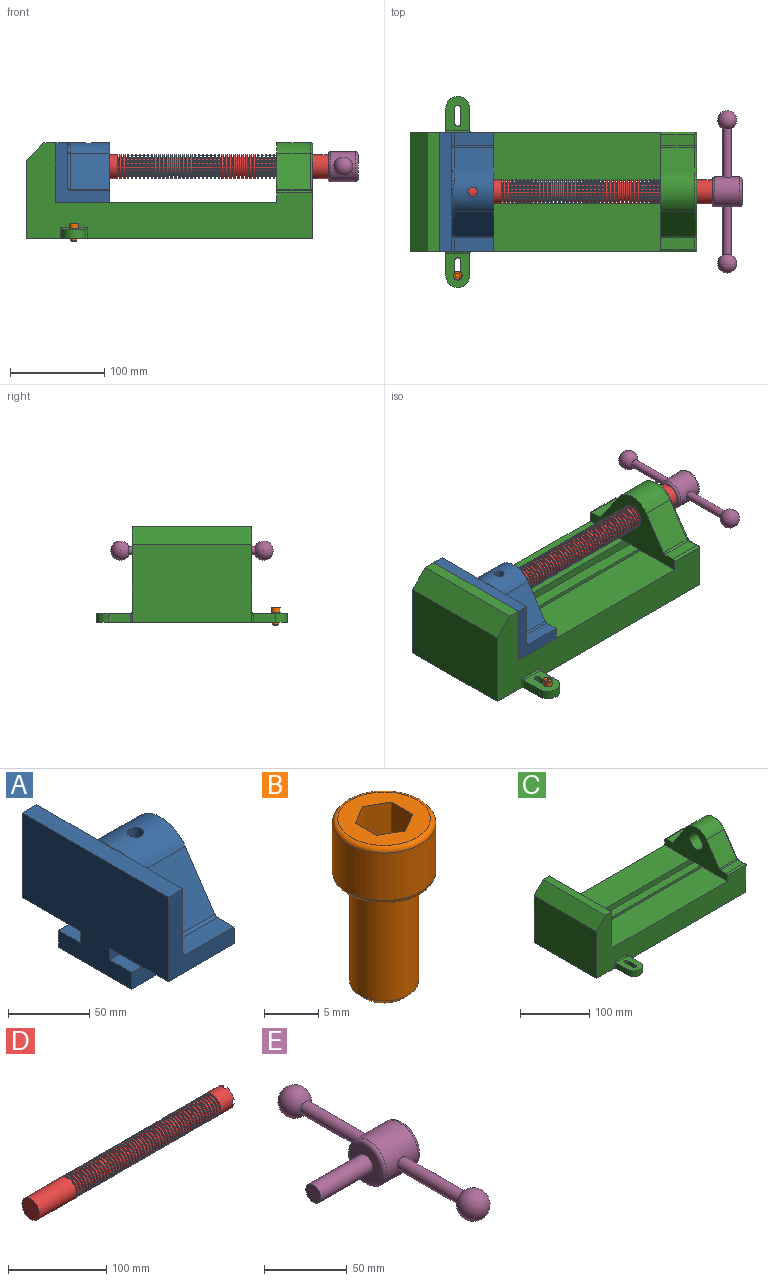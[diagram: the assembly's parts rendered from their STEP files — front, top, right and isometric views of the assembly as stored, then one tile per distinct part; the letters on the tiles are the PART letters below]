
ASSEMBLY  parts=5 mates=5
PART A: 36 faces, bbox 57.2x127x89 mm
  f0: plane 57.15x50.8mm, normal (0,0,-1), area 2903.2mm2, adj f6,f9,f10,f23
  f1: cylinder r=12.7mm len=44.45mm, axis (1,0,0), area 3464.3mm2, adj f6,f15,f16
  f2: plane 41.91x14.52mm, normal (0,0,1), area 608.5mm2, adj f6,f11,f24,f25
  f3: plane 51.86x48.26mm, normal (1,0,0), area 1495.7mm2, adj f8,f10,f31,f33,f35
  f4: plane 51.86x48.26mm, normal (1,0,0), area 1495.7mm2, adj f8,f11,f24,f28,f29
  f5: plane 57.15x50.8mm, normal (0,0,-1), area 2903.2mm2, adj f6,f9,f11,f22
  f6: plane 127x85.09mm, normal (1,0,0), area 5190.6mm2, adj f0,f1,f2,f5,f7,f10,f11,f12
  f7: plane 41.91x14.52mm, normal (0,0,1), area 608.5mm2, adj f6,f10,f30,f31
  f8: plane 127x12.7mm, normal (0,0,1), area 1612.9mm2, adj f3,f4,f9,f10,f11,f26,f34
  f9: plane 127x85.09mm, normal (-1,0,0), area 9096.8mm2, adj f0,f5,f8,f10,f11,f17,f18,f19
  f10: plane 63.5x57.15mm, normal (0,-1,0), area 1372.3mm2, adj f0,f3,f6,f7,f8,f9,f31
  f11: plane 63.5x57.15mm, normal (0,1,0), area 1372.3mm2, adj f2,f4,f5,f6,f8,f9,f24
  f12: plane 41.91x38.43mm, normal (0,-0.83,0.56), area 1939.2mm2, adj f6,f13,f30,f33
  f13: cylinder r=25.4mm len=44.45mm, axis (1,0,0), area 2026.5mm2, adj f6,f12,f14,f16,f26,f28,f34,f35
  f14: plane 41.91x38.43mm, normal (0,0.83,0.56), area 1939.2mm2, adj f6,f13,f25,f29
  f15: plane 25.4x25.4mm, normal (1,0,0), area 506.7mm2, adj f1
  f16: cylinder r=5.08mm len=13.76mm, axis (0,0,1), area 414mm2, adj f1,f13
  f17: plane 57.15x19.05mm, normal (0,0,1), area 1088.7mm2, adj f6,f9,f18,f23
  f18: plane 57.15x12.7mm, normal (0,-1,0), area 725.8mm2, adj f6,f9,f17,f19
  f19: plane 63.5x57.15mm, normal (0,0,-1), area 3629mm2, adj f6,f9,f18,f20
  f20: plane 57.15x12.7mm, normal (0,1,0), area 725.8mm2, adj f6,f9,f19,f21
  f21: plane 57.15x19.05mm, normal (0,0,1), area 1088.7mm2, adj f6,f9,f20,f22
  f22: plane 57.15x8.89mm, normal (0,1,0), area 508.1mm2, adj f5,f6,f9,f21
  f23: plane 57.15x8.89mm, normal (0,-1,0), area 508.1mm2, adj f0,f6,f9,f17
  f24: cylinder r=2.54mm len=14.52mm, axis (0,-1,0), area 57.9mm2, adj f2,f4,f11,f27
  f25: cylinder r=2.54mm len=41.91mm, axis (1,0,0), area 104.3mm2, adj f2,f6,f14,f27
  f26: bspline ~12.24x2.8mm, area 20.9mm2, adj f8,f13,f28
  f27: sphere r=2.54mm, area 6.3mm2, adj f24,f25,f29
  f28: torus R=27.94mm, axis (1,0,0), area 57.8mm2, adj f4,f13,f26,f29
  f29: cylinder r=2.54mm len=39.84mm, axis (0,-0.56,0.83), area 184.6mm2, adj f4,f14,f27,f28
  f30: cylinder r=2.54mm len=41.91mm, axis (1,0,0), area 104.3mm2, adj f6,f7,f12,f32
  f31: cylinder r=2.54mm len=14.52mm, axis (0,-1,0), area 57.9mm2, adj f3,f7,f10,f32
  f32: sphere r=2.54mm, area 6.3mm2, adj f30,f31,f33
  f33: cylinder r=2.54mm len=39.84mm, axis (0,-0.56,-0.83), area 184.6mm2, adj f3,f12,f32,f35
  f34: bspline ~12.24x2.8mm, area 20.9mm2, adj f8,f13,f35
  f35: torus R=27.94mm, axis (1,0,0), area 57.8mm2, adj f3,f13,f33,f34
PART B: 15 faces, bbox 10.3x10.3x19.1 mm
  f0: plane 8.51x8.51mm, normal (0,0,1), area 37.2mm2, adj f5,f6,f7,f8,f9,f10,f14
  f1: cylinder r=3.17mm len=11.94mm, axis (0,0,1), area 238.2mm2, adj f4,f12
  f2: plane 4.83x4.83mm, normal (0,0,-1), area 18.3mm2, adj f12
  f3: cylinder r=4.76mm len=9.53mm, axis (0,0,-1), area 159.6mm2, adj f13,f14
  f4: plane 8.51x8.51mm, normal (0,0,-1), area 25.2mm2, adj f1,f13
  f5: plane 4.83x2.38mm, normal (-0.5,-0.87,0), area 13.3mm2, adj f0,f6,f10,f11
  f6: plane 4.83x2.38mm, normal (0.5,-0.87,0), area 13.3mm2, adj f0,f5,f7,f11
  f7: plane 4.83x2.75mm, normal (1,0,0), area 13.3mm2, adj f0,f6,f8,f11
  f8: plane 4.83x2.38mm, normal (0.5,0.87,0), area 13.3mm2, adj f0,f7,f9,f11
  f9: plane 4.83x2.38mm, normal (-0.5,0.87,0), area 13.3mm2, adj f0,f8,f10,f11
  f10: plane 4.83x2.75mm, normal (-1,0,0), area 13.3mm2, adj f0,f5,f9,f11
  f11: plane 5.5x4.76mm, normal (0,0,1), area 19.6mm2, adj f5,f6,f7,f8,f9,f10
  f12: cone r=3.17mm half-angle=45deg, axis (0,0,1), area 18.9mm2, adj f1,f2
  f13: torus R=4.25mm, axis (0,0,1), area 23mm2, adj f3,f4
  f14: torus R=4.25mm, axis (0,0,1), area 23mm2, adj f0,f3
PART C: 61 faces, bbox 304.8x203.2x103.7 mm
  f0: plane 304.8x101.6mm, normal (0,1,0), area 13520.3mm2, adj f3,f4,f5,f6,f7,f8,f9,f16
  f1: plane 304.8x101.6mm, normal (0,-1,0), area 13520.3mm2, adj f2,f3,f5,f6,f7,f8,f9,f16
  f2: plane 234.95x50.8mm, normal (0,0,1), area 11935.5mm2, adj f1,f5,f16,f26
  f3: plane 127x99.06mm, normal (1,0,0), area 7097.5mm2, adj f0,f1,f9,f14,f17,f18,f19,f20
  f4: plane 234.95x50.8mm, normal (0,0,1), area 11935.5mm2, adj f0,f5,f16,f27
  f5: plane 127x101.6mm, normal (1,0,0), area 9516.1mm2, adj f0,f1,f2,f4,f6,f9,f18,f19
  f6: plane 127x12.7mm, normal (0,0,1), area 1612.9mm2, adj f0,f1,f5,f7
  f7: plane 127x19.05mm, normal (-0.71,0,0.71), area 3421.5mm2, adj f0,f1,f6,f8
  f8: plane 127x82.55mm, normal (-1,0,0), area 10483.8mm2, adj f0,f1,f7,f9
  f9: plane 304.8x203.2mm, normal (0,0,-1), area 33298.3mm2, adj f0,f1,f3,f5,f8,f21,f22,f39
  f10: plane 35.56x11.98mm, normal (0,0,1), area 426mm2, adj f16,f28,f29,f30
  f11: plane 38.43x35.56mm, normal (0,0.83,0.56), area 1645.4mm2, adj f12,f16,f29,f32
  f12: cylinder r=25.4mm len=42.19mm, axis (1,0,0), area 1770.2mm2, adj f11,f13,f16,f33
  f13: plane 38.43x35.56mm, normal (0,-0.83,0.56), area 1645.4mm2, adj f12,f16,f34,f35
  f14: cylinder r=12.7mm len=38.1mm, axis (1,0,0), area 3040.2mm2, adj f3,f16
  f15: plane 35.56x11.98mm, normal (0,0,1), area 426mm2, adj f16,f34,f36,f38
  f16: plane 127x63.5mm, normal (-1,0,0), area 4155.5mm2, adj f0,f1,f2,f4,f10,f11,f12,f13
  f17: plane 38.1x25.4mm, normal (0,0,-1), area 967.7mm2, adj f3,f16,f26,f27
  f18: plane 273.05x19.05mm, normal (0,0,-1), area 5201.6mm2, adj f3,f5,f19,f26
  f19: plane 273.05x12.7mm, normal (0,1,0), area 3467.7mm2, adj f3,f5,f18,f20
  f20: plane 273.05x19.05mm, normal (0,0,1), area 5201.6mm2, adj f3,f5,f19,f21
  f21: plane 273.05x16.51mm, normal (0,1,0), area 4508.1mm2, adj f3,f5,f9,f20
  f22: plane 273.05x16.51mm, normal (0,-1,0), area 4508.1mm2, adj f3,f5,f9,f23
  f23: plane 273.05x19.05mm, normal (0,0,1), area 5201.6mm2, adj f3,f5,f22,f24
  f24: plane 273.05x12.7mm, normal (0,-1,0), area 3467.7mm2, adj f3,f5,f23,f25
  f25: plane 273.05x19.05mm, normal (0,0,-1), area 5201.6mm2, adj f3,f5,f24,f27
  f26: plane 273.05x8.89mm, normal (0,1,0), area 2427.4mm2, adj f2,f3,f5,f17,f18
  f27: plane 273.05x8.89mm, normal (0,-1,0), area 2427.4mm2, adj f3,f4,f5,f17,f25
  f28: cylinder r=2.54mm len=38.1mm, axis (1,0,0), area 148.3mm2, adj f0,f10,f16,f30
  f29: cylinder r=2.54mm len=35.56mm, axis (-1,0,0), area 88.5mm2, adj f10,f11,f16,f31
  f30: cylinder r=2.54mm len=14.52mm, axis (0,1,0), area 54.3mm2, adj f3,f10,f28,f31
  f31: torus R=5.08mm, axis (-1,0,0), area 13.5mm2, adj f3,f29,f30,f32
  f32: cylinder r=2.54mm len=39.84mm, axis (0,0.56,-0.83), area 184.6mm2, adj f3,f11,f31,f33
  f33: torus R=22.86mm, axis (-1,0,0), area 191.4mm2, adj f3,f12,f32,f35
  f34: cylinder r=2.54mm len=35.56mm, axis (-1,0,0), area 88.5mm2, adj f13,f15,f16,f37
  f35: cylinder r=2.54mm len=39.84mm, axis (0,0.56,0.83), area 184.6mm2, adj f3,f13,f33,f37
  f36: cylinder r=2.54mm len=38.1mm, axis (-1,0,0), area 148.3mm2, adj f1,f15,f16,f38
  f37: torus R=5.08mm, axis (-1,0,0), area 13.5mm2, adj f3,f34,f35,f38
  f38: cylinder r=2.54mm len=14.52mm, axis (0,1,0), area 54.3mm2, adj f3,f15,f36,f37
  f39: plane 23.88x9.53mm, normal (-1,0,0), area 227.4mm2, adj f9,f45,f46,f60
  f40: plane 23.88x9.53mm, normal (1,0,0), area 227.4mm2, adj f9,f45,f46,f58
  f41: cylinder r=3.3mm len=9.53mm, axis (0,0,-1), area 98.8mm2, adj f9,f42,f44,f46
  f42: plane 15.62x9.53mm, normal (-1,0,0), area 148.8mm2, adj f9,f41,f43,f46
  f43: cylinder r=3.3mm len=9.53mm, axis (0,0,-1), area 98.8mm2, adj f9,f42,f44,f46
  f44: plane 15.62x9.53mm, normal (1,0,0), area 148.8mm2, adj f9,f41,f43,f46
  f45: cylinder r=12.7mm len=25.4mm, axis (0,0,-1), area 380mm2, adj f9,f39,f40,f46
  f46: plane 36.58x25.4mm, normal (0,0,1), area 722.4mm2, adj f39,f40,f41,f42,f43,f44,f45,f59
  f47: plane 23.88x9.53mm, normal (-1,0,0), area 227.4mm2, adj f9,f53,f54,f56
  f48: plane 23.88x9.53mm, normal (1,0,0), area 227.4mm2, adj f9,f53,f54,f55
  f49: cylinder r=3.3mm len=9.53mm, axis (0,0,-1), area 98.8mm2, adj f9,f50,f52,f54
  f50: plane 15.62x9.53mm, normal (-1,0,0), area 148.8mm2, adj f9,f49,f51,f54
  f51: cylinder r=3.3mm len=9.53mm, axis (0,0,-1), area 98.8mm2, adj f9,f50,f52,f54
  f52: plane 15.62x9.53mm, normal (1,0,0), area 148.8mm2, adj f9,f49,f51,f54
  f53: cylinder r=12.7mm len=25.4mm, axis (0,0,-1), area 380mm2, adj f9,f47,f48,f54
  f54: plane 36.58x25.4mm, normal (0,0,1), area 722.4mm2, adj f47,f48,f49,f50,f51,f52,f53,f57
  f55: cylinder r=1.52mm len=11.05mm, axis (0,0,-1), area 24.1mm2, adj f0,f9,f48,f57
  f56: cylinder r=1.52mm len=11.05mm, axis (0,0,1), area 24.1mm2, adj f0,f9,f47,f57
  f57: cylinder r=1.52mm len=28.45mm, axis (1,0,0), area 63.5mm2, adj f0,f54,f55,f56
  f58: cylinder r=1.52mm len=11.05mm, axis (0,0,1), area 24.1mm2, adj f1,f9,f40,f59
  f59: cylinder r=1.52mm len=28.45mm, axis (-1,0,0), area 63.5mm2, adj f1,f46,f58,f60
  f60: cylinder r=1.52mm len=11.05mm, axis (0,0,-1), area 24.1mm2, adj f1,f9,f39,f59
PART D: 220 faces, bbox 279.4x25.4x25.4 mm
  f0: cylinder r=12.7mm len=25.4mm, axis (-1,0,0), area 1468.2mm2, adj f1,f2,f3,f5,f7,f208,f209,f210
  f1: plane 9.9x9.9mm, normal (1,0,0), area 62.3mm2, adj f0,f4,f213,f216
  f2: plane 9.9x9.9mm, normal (1,0,0), area 62.3mm2, adj f0,f4,f210,f218
  f3: plane 9.9x9.9mm, normal (1,0,0), area 62.3mm2, adj f0,f4,f209,f212
  f4: cylinder r=6.35mm len=25.4mm, axis (1,0,0), area 960.3mm2, adj f1,f2,f3,f5,f6,f208,f209,f210
  f5: plane 9.9x9.9mm, normal (1,0,0), area 62.3mm2, adj f0,f4,f215,f217
  f6: plane 12.7x12.7mm, normal (1,0,0), area 126.7mm2, adj f4
  f7: cone r=12.7mm half-angle=76deg, axis (1,0,0), area 188mm2, adj f0,f9
  f8: cone r=10.16mm half-angle=76deg, axis (-1,0,0), area 188mm2, adj f9,f10
  f9: cylinder r=10.16mm len=20.32mm, axis (1,0,0), area 81.1mm2, adj f7,f8
  f10: cylinder r=12.7mm len=25.4mm, axis (-1,0,0), area 131.7mm2, adj f8,f11
  f11: cone r=12.7mm half-angle=76deg, axis (1,0,0), area 188mm2, adj f10,f13
  f12: cone r=10.16mm half-angle=76deg, axis (-1,0,0), area 188mm2, adj f13,f14
  f13: cylinder r=10.16mm len=20.32mm, axis (1,0,0), area 81.1mm2, adj f11,f12
  f14: cylinder r=12.7mm len=25.4mm, axis (-1,0,0), area 131.7mm2, adj f12,f15
  f15: cone r=12.7mm half-angle=76deg, axis (1,0,0), area 188mm2, adj f14,f17
  f16: cone r=10.16mm half-angle=76deg, axis (-1,0,0), area 188mm2, adj f17,f18
  f17: cylinder r=10.16mm len=20.32mm, axis (1,0,0), area 81.1mm2, adj f15,f16
  f18: cylinder r=12.7mm len=25.4mm, axis (-1,0,0), area 131.7mm2, adj f16,f19
  f19: cone r=12.7mm half-angle=76deg, axis (1,0,0), area 188mm2, adj f18,f21
  f20: cone r=10.16mm half-angle=76deg, axis (-1,0,0), area 188mm2, adj f21,f22
  f21: cylinder r=10.16mm len=20.32mm, axis (1,0,0), area 81.1mm2, adj f19,f20
  f22: cylinder r=12.7mm len=25.4mm, axis (-1,0,0), area 131.7mm2, adj f20,f23
  f23: cone r=12.7mm half-angle=76deg, axis (1,0,0), area 188mm2, adj f22,f25
  f24: cone r=10.16mm half-angle=76deg, axis (-1,0,0), area 188mm2, adj f25,f26
  f25: cylinder r=10.16mm len=20.32mm, axis (1,0,0), area 81.1mm2, adj f23,f24
  f26: cylinder r=12.7mm len=25.4mm, axis (-1,0,0), area 131.7mm2, adj f24,f27
  f27: cone r=12.7mm half-angle=76deg, axis (1,0,0), area 188mm2, adj f26,f29
  f28: cone r=10.16mm half-angle=76deg, axis (-1,0,0), area 188mm2, adj f29,f30
  f29: cylinder r=10.16mm len=20.32mm, axis (1,0,0), area 81.1mm2, adj f27,f28
  f30: cylinder r=12.7mm len=25.4mm, axis (-1,0,0), area 131.7mm2, adj f28,f31
  f31: cone r=12.7mm half-angle=76deg, axis (1,0,0), area 188mm2, adj f30,f33
  f32: cone r=10.16mm half-angle=76deg, axis (-1,0,0), area 188mm2, adj f33,f34
  f33: cylinder r=10.16mm len=20.32mm, axis (1,0,0), area 81.1mm2, adj f31,f32
  f34: cylinder r=12.7mm len=25.4mm, axis (-1,0,0), area 131.7mm2, adj f32,f35
  f35: cone r=12.7mm half-angle=76deg, axis (1,0,0), area 188mm2, adj f34,f37
  f36: cone r=10.16mm half-angle=76deg, axis (-1,0,0), area 188mm2, adj f37,f38
  f37: cylinder r=10.16mm len=20.32mm, axis (1,0,0), area 81.1mm2, adj f35,f36
  f38: cylinder r=12.7mm len=25.4mm, axis (-1,0,0), area 131.7mm2, adj f36,f39
  f39: cone r=12.7mm half-angle=76deg, axis (1,0,0), area 188mm2, adj f38,f41
  f40: cone r=10.16mm half-angle=76deg, axis (-1,0,0), area 188mm2, adj f41,f42
  f41: cylinder r=10.16mm len=20.32mm, axis (1,0,0), area 81.1mm2, adj f39,f40
  f42: cylinder r=12.7mm len=25.4mm, axis (-1,0,0), area 131.7mm2, adj f40,f43
  f43: cone r=12.7mm half-angle=76deg, axis (1,0,0), area 188mm2, adj f42,f45
  f44: cone r=10.16mm half-angle=76deg, axis (-1,0,0), area 188mm2, adj f45,f46
  f45: cylinder r=10.16mm len=20.32mm, axis (1,0,0), area 81.1mm2, adj f43,f44
  f46: cylinder r=12.7mm len=25.4mm, axis (-1,0,0), area 131.7mm2, adj f44,f47
  f47: cone r=12.7mm half-angle=76deg, axis (1,0,0), area 188mm2, adj f46,f49
  f48: cone r=10.16mm half-angle=76deg, axis (-1,0,0), area 188mm2, adj f49,f50
  f49: cylinder r=10.16mm len=20.32mm, axis (1,0,0), area 81.1mm2, adj f47,f48
  f50: cylinder r=12.7mm len=25.4mm, axis (-1,0,0), area 131.7mm2, adj f48,f51
  f51: cone r=12.7mm half-angle=76deg, axis (1,0,0), area 188mm2, adj f50,f53
  f52: cone r=10.16mm half-angle=76deg, axis (-1,0,0), area 188mm2, adj f53,f54
  f53: cylinder r=10.16mm len=20.32mm, axis (1,0,0), area 81.1mm2, adj f51,f52
  f54: cylinder r=12.7mm len=25.4mm, axis (-1,0,0), area 131.7mm2, adj f52,f55
  f55: cone r=12.7mm half-angle=76deg, axis (1,0,0), area 188mm2, adj f54,f57
  f56: cone r=10.16mm half-angle=76deg, axis (-1,0,0), area 188mm2, adj f57,f58
  f57: cylinder r=10.16mm len=20.32mm, axis (1,0,0), area 81.1mm2, adj f55,f56
  f58: cylinder r=12.7mm len=25.4mm, axis (-1,0,0), area 131.7mm2, adj f56,f59
  f59: cone r=12.7mm half-angle=76deg, axis (1,0,0), area 188mm2, adj f58,f61
  f60: cone r=10.16mm half-angle=76deg, axis (-1,0,0), area 188mm2, adj f61,f62
  f61: cylinder r=10.16mm len=20.32mm, axis (1,0,0), area 81.1mm2, adj f59,f60
  f62: cylinder r=12.7mm len=25.4mm, axis (-1,0,0), area 131.7mm2, adj f60,f63
  f63: cone r=12.7mm half-angle=76deg, axis (1,0,0), area 188mm2, adj f62,f65
  f64: cone r=10.16mm half-angle=76deg, axis (-1,0,0), area 188mm2, adj f65,f66
  f65: cylinder r=10.16mm len=20.32mm, axis (1,0,0), area 81.1mm2, adj f63,f64
  f66: cylinder r=12.7mm len=25.4mm, axis (-1,0,0), area 131.7mm2, adj f64,f67
  f67: cone r=12.7mm half-angle=76deg, axis (1,0,0), area 188mm2, adj f66,f69
  f68: cone r=10.16mm half-angle=76deg, axis (-1,0,0), area 188mm2, adj f69,f70
  f69: cylinder r=10.16mm len=20.32mm, axis (1,0,0), area 81.1mm2, adj f67,f68
  f70: cylinder r=12.7mm len=25.4mm, axis (-1,0,0), area 131.7mm2, adj f68,f71
  f71: cone r=12.7mm half-angle=76deg, axis (1,0,0), area 188mm2, adj f70,f73
  f72: cone r=10.16mm half-angle=76deg, axis (-1,0,0), area 188mm2, adj f73,f74
  f73: cylinder r=10.16mm len=20.32mm, axis (1,0,0), area 81.1mm2, adj f71,f72
  f74: cylinder r=12.7mm len=25.4mm, axis (-1,0,0), area 131.7mm2, adj f72,f75
  f75: cone r=12.7mm half-angle=76deg, axis (1,0,0), area 188mm2, adj f74,f77
  f76: cone r=10.16mm half-angle=76deg, axis (-1,0,0), area 188mm2, adj f77,f78
  f77: cylinder r=10.16mm len=20.32mm, axis (1,0,0), area 81.1mm2, adj f75,f76
  f78: cylinder r=12.7mm len=25.4mm, axis (-1,0,0), area 131.7mm2, adj f76,f79
  f79: cone r=12.7mm half-angle=76deg, axis (1,0,0), area 188mm2, adj f78,f81
  f80: cone r=10.16mm half-angle=76deg, axis (-1,0,0), area 188mm2, adj f81,f82
  f81: cylinder r=10.16mm len=20.32mm, axis (1,0,0), area 81.1mm2, adj f79,f80
  f82: cylinder r=12.7mm len=25.4mm, axis (-1,0,0), area 131.7mm2, adj f80,f83
  f83: cone r=12.7mm half-angle=76deg, axis (1,0,0), area 188mm2, adj f82,f85
  f84: cone r=10.16mm half-angle=76deg, axis (-1,0,0), area 188mm2, adj f85,f86
  f85: cylinder r=10.16mm len=20.32mm, axis (1,0,0), area 81.1mm2, adj f83,f84
  f86: cylinder r=12.7mm len=25.4mm, axis (-1,0,0), area 131.7mm2, adj f84,f87
  f87: cone r=12.7mm half-angle=76deg, axis (1,0,0), area 188mm2, adj f86,f89
  f88: cone r=10.16mm half-angle=76deg, axis (-1,0,0), area 188mm2, adj f89,f90
  f89: cylinder r=10.16mm len=20.32mm, axis (1,0,0), area 81.1mm2, adj f87,f88
  f90: cylinder r=12.7mm len=25.4mm, axis (-1,0,0), area 131.7mm2, adj f88,f91
  f91: cone r=12.7mm half-angle=76deg, axis (1,0,0), area 188mm2, adj f90,f93
  f92: cone r=10.16mm half-angle=76deg, axis (-1,0,0), area 188mm2, adj f93,f94
  f93: cylinder r=10.16mm len=20.32mm, axis (1,0,0), area 81.1mm2, adj f91,f92
  f94: cylinder r=12.7mm len=25.4mm, axis (-1,0,0), area 131.7mm2, adj f92,f95
  f95: cone r=12.7mm half-angle=76deg, axis (1,0,0), area 188mm2, adj f94,f97
  f96: cone r=10.16mm half-angle=76deg, axis (-1,0,0), area 188mm2, adj f97,f98
  f97: cylinder r=10.16mm len=20.32mm, axis (1,0,0), area 81.1mm2, adj f95,f96
  f98: cylinder r=12.7mm len=25.4mm, axis (-1,0,0), area 131.7mm2, adj f96,f99
  f99: cone r=12.7mm half-angle=76deg, axis (1,0,0), area 188mm2, adj f98,f101
  f100: cone r=10.16mm half-angle=76deg, axis (-1,0,0), area 188mm2, adj f101,f102
  f101: cylinder r=10.16mm len=20.32mm, axis (1,0,0), area 81.1mm2, adj f99,f100
  f102: cylinder r=12.7mm len=25.4mm, axis (-1,0,0), area 131.7mm2, adj f100,f103
  f103: cone r=12.7mm half-angle=76deg, axis (1,0,0), area 188mm2, adj f102,f105
  f104: cone r=10.16mm half-angle=76deg, axis (-1,0,0), area 188mm2, adj f105,f106
  f105: cylinder r=10.16mm len=20.32mm, axis (1,0,0), area 81.1mm2, adj f103,f104
  f106: cylinder r=12.7mm len=25.4mm, axis (-1,0,0), area 131.7mm2, adj f104,f107
  f107: cone r=12.7mm half-angle=76deg, axis (1,0,0), area 188mm2, adj f106,f109
  f108: cone r=10.16mm half-angle=76deg, axis (-1,0,0), area 188mm2, adj f109,f110
  f109: cylinder r=10.16mm len=20.32mm, axis (1,0,0), area 81.1mm2, adj f107,f108
  f110: cylinder r=12.7mm len=25.4mm, axis (-1,0,0), area 131.7mm2, adj f108,f111
  f111: cone r=12.7mm half-angle=76deg, axis (1,0,0), area 188mm2, adj f110,f113
  f112: cone r=10.16mm half-angle=76deg, axis (-1,0,0), area 188mm2, adj f113,f114
  f113: cylinder r=10.16mm len=20.32mm, axis (1,0,0), area 81.1mm2, adj f111,f112
  f114: cylinder r=12.7mm len=25.4mm, axis (-1,0,0), area 131.7mm2, adj f112,f115
  f115: cone r=12.7mm half-angle=76deg, axis (1,0,0), area 188mm2, adj f114,f117
  f116: cone r=10.16mm half-angle=76deg, axis (-1,0,0), area 188mm2, adj f117,f118
  f117: cylinder r=10.16mm len=20.32mm, axis (1,0,0), area 81.1mm2, adj f115,f116
  f118: cylinder r=12.7mm len=25.4mm, axis (-1,0,0), area 131.7mm2, adj f116,f119
  f119: cone r=12.7mm half-angle=76deg, axis (1,0,0), area 188mm2, adj f118,f121
  f120: cone r=10.16mm half-angle=76deg, axis (-1,0,0), area 188mm2, adj f121,f122
  f121: cylinder r=10.16mm len=20.32mm, axis (1,0,0), area 81.1mm2, adj f119,f120
  f122: cylinder r=12.7mm len=25.4mm, axis (-1,0,0), area 131.7mm2, adj f120,f123
  f123: cone r=12.7mm half-angle=76deg, axis (1,0,0), area 188mm2, adj f122,f125
  f124: cone r=10.16mm half-angle=76deg, axis (-1,0,0), area 188mm2, adj f125,f126
  f125: cylinder r=10.16mm len=20.32mm, axis (1,0,0), area 81.1mm2, adj f123,f124
  f126: cylinder r=12.7mm len=25.4mm, axis (-1,0,0), area 131.7mm2, adj f124,f127
  f127: cone r=12.7mm half-angle=76deg, axis (1,0,0), area 188mm2, adj f126,f129
  f128: cone r=10.16mm half-angle=76deg, axis (-1,0,0), area 188mm2, adj f129,f130
  f129: cylinder r=10.16mm len=20.32mm, axis (1,0,0), area 81.1mm2, adj f127,f128
  f130: cylinder r=12.7mm len=25.4mm, axis (-1,0,0), area 131.7mm2, adj f128,f131
  f131: cone r=12.7mm half-angle=76deg, axis (1,0,0), area 188mm2, adj f130,f133
  f132: cone r=10.16mm half-angle=76deg, axis (-1,0,0), area 188mm2, adj f133,f134
  f133: cylinder r=10.16mm len=20.32mm, axis (1,0,0), area 81.1mm2, adj f131,f132
  f134: cylinder r=12.7mm len=25.4mm, axis (-1,0,0), area 131.7mm2, adj f132,f135
  f135: cone r=12.7mm half-angle=76deg, axis (1,0,0), area 188mm2, adj f134,f137
  f136: cone r=10.16mm half-angle=76deg, axis (-1,0,0), area 188mm2, adj f137,f138
  f137: cylinder r=10.16mm len=20.32mm, axis (1,0,0), area 81.1mm2, adj f135,f136
  f138: cylinder r=12.7mm len=25.4mm, axis (-1,0,0), area 131.7mm2, adj f136,f139
  f139: cone r=12.7mm half-angle=76deg, axis (1,0,0), area 188mm2, adj f138,f141
  f140: cone r=10.16mm half-angle=76deg, axis (-1,0,0), area 188mm2, adj f141,f142
  f141: cylinder r=10.16mm len=20.32mm, axis (1,0,0), area 81.1mm2, adj f139,f140
  f142: cylinder r=12.7mm len=25.4mm, axis (-1,0,0), area 131.7mm2, adj f140,f143
  f143: cone r=12.7mm half-angle=76deg, axis (1,0,0), area 188mm2, adj f142,f145
  f144: cone r=10.16mm half-angle=76deg, axis (-1,0,0), area 188mm2, adj f145,f146
  f145: cylinder r=10.16mm len=20.32mm, axis (1,0,0), area 81.1mm2, adj f143,f144
  f146: cylinder r=12.7mm len=25.4mm, axis (-1,0,0), area 131.7mm2, adj f144,f147
  f147: cone r=12.7mm half-angle=76deg, axis (1,0,0), area 188mm2, adj f146,f149
  f148: cone r=10.16mm half-angle=76deg, axis (-1,0,0), area 188mm2, adj f149,f150
  f149: cylinder r=10.16mm len=20.32mm, axis (1,0,0), area 81.1mm2, adj f147,f148
  f150: cylinder r=12.7mm len=25.4mm, axis (-1,0,0), area 131.7mm2, adj f148,f151
  f151: cone r=12.7mm half-angle=76deg, axis (1,0,0), area 188mm2, adj f150,f153
  f152: cone r=10.16mm half-angle=76deg, axis (-1,0,0), area 188mm2, adj f153,f154
  f153: cylinder r=10.16mm len=20.32mm, axis (1,0,0), area 81.1mm2, adj f151,f152
  f154: cylinder r=12.7mm len=25.4mm, axis (-1,0,0), area 131.7mm2, adj f152,f155
  f155: cone r=12.7mm half-angle=76deg, axis (1,0,0), area 188mm2, adj f154,f157
  f156: cone r=10.16mm half-angle=76deg, axis (-1,0,0), area 188mm2, adj f157,f158
  f157: cylinder r=10.16mm len=20.32mm, axis (1,0,0), area 81.1mm2, adj f155,f156
  f158: cylinder r=12.7mm len=25.4mm, axis (-1,0,0), area 131.7mm2, adj f156,f159
  f159: cone r=12.7mm half-angle=76deg, axis (1,0,0), area 188mm2, adj f158,f161
  f160: cone r=10.16mm half-angle=76deg, axis (-1,0,0), area 188mm2, adj f161,f162
  f161: cylinder r=10.16mm len=20.32mm, axis (1,0,0), area 81.1mm2, adj f159,f160
  f162: cylinder r=12.7mm len=25.4mm, axis (-1,0,0), area 131.7mm2, adj f160,f163
  f163: cone r=12.7mm half-angle=76deg, axis (1,0,0), area 188mm2, adj f162,f165
  f164: cone r=10.16mm half-angle=76deg, axis (-1,0,0), area 188mm2, adj f165,f166
  f165: cylinder r=10.16mm len=20.32mm, axis (1,0,0), area 81.1mm2, adj f163,f164
  f166: cylinder r=12.7mm len=25.4mm, axis (-1,0,0), area 131.7mm2, adj f164,f167
  f167: cone r=12.7mm half-angle=76deg, axis (1,0,0), area 188mm2, adj f166,f169
  f168: cone r=10.16mm half-angle=76deg, axis (-1,0,0), area 188mm2, adj f169,f170
  f169: cylinder r=10.16mm len=20.32mm, axis (1,0,0), area 81.1mm2, adj f167,f168
  f170: cylinder r=12.7mm len=25.4mm, axis (-1,0,0), area 131.7mm2, adj f168,f171
  f171: cone r=12.7mm half-angle=76deg, axis (1,0,0), area 188mm2, adj f170,f173
  f172: cone r=10.16mm half-angle=76deg, axis (-1,0,0), area 188mm2, adj f173,f174
  f173: cylinder r=10.16mm len=20.32mm, axis (1,0,0), area 81.1mm2, adj f171,f172
  f174: cylinder r=12.7mm len=25.4mm, axis (-1,0,0), area 131.7mm2, adj f172,f175
  f175: cone r=12.7mm half-angle=76deg, axis (1,0,0), area 188mm2, adj f174,f177
  f176: cone r=10.16mm half-angle=76deg, axis (-1,0,0), area 188mm2, adj f177,f178
  f177: cylinder r=10.16mm len=20.32mm, axis (1,0,0), area 81.1mm2, adj f175,f176
  f178: cylinder r=12.7mm len=25.4mm, axis (-1,0,0), area 131.7mm2, adj f176,f179
  f179: cone r=12.7mm half-angle=76deg, axis (1,0,0), area 188mm2, adj f178,f181
  f180: cone r=10.16mm half-angle=76deg, axis (-1,0,0), area 188mm2, adj f181,f182
  f181: cylinder r=10.16mm len=20.32mm, axis (1,0,0), area 81.1mm2, adj f179,f180
  f182: cylinder r=12.7mm len=25.4mm, axis (-1,0,0), area 131.7mm2, adj f180,f183
  f183: cone r=12.7mm half-angle=76deg, axis (1,0,0), area 188mm2, adj f182,f185
  f184: cone r=10.16mm half-angle=76deg, axis (-1,0,0), area 188mm2, adj f185,f186
  f185: cylinder r=10.16mm len=20.32mm, axis (1,0,0), area 81.1mm2, adj f183,f184
  f186: cylinder r=12.7mm len=25.4mm, axis (-1,0,0), area 131.7mm2, adj f184,f187
  f187: cone r=12.7mm half-angle=76deg, axis (1,0,0), area 188mm2, adj f186,f189
  f188: cone r=10.16mm half-angle=76deg, axis (-1,0,0), area 188mm2, adj f189,f190
  f189: cylinder r=10.16mm len=20.32mm, axis (1,0,0), area 81.1mm2, adj f187,f188
  f190: cylinder r=12.7mm len=25.4mm, axis (-1,0,0), area 131.7mm2, adj f188,f191
  f191: cone r=12.7mm half-angle=76deg, axis (1,0,0), area 188mm2, adj f190,f193
  f192: cone r=10.16mm half-angle=76deg, axis (-1,0,0), area 188mm2, adj f193,f194
  f193: cylinder r=10.16mm len=20.32mm, axis (1,0,0), area 81.1mm2, adj f191,f192
  f194: cylinder r=12.7mm len=25.4mm, axis (-1,0,0), area 131.7mm2, adj f192,f195
  f195: cone r=12.7mm half-angle=76deg, axis (1,0,0), area 188mm2, adj f194,f197
  f196: cone r=10.16mm half-angle=76deg, axis (-1,0,0), area 188mm2, adj f197,f198
  f197: cylinder r=10.16mm len=20.32mm, axis (1,0,0), area 81.1mm2, adj f195,f196
  f198: cylinder r=12.7mm len=25.4mm, axis (-1,0,0), area 131.7mm2, adj f196,f199
  f199: cone r=12.7mm half-angle=76deg, axis (1,0,0), area 188mm2, adj f198,f201
  f200: cone r=10.16mm half-angle=76deg, axis (-1,0,0), area 188mm2, adj f201,f202
  f201: cylinder r=10.16mm len=20.32mm, axis (1,0,0), area 81.1mm2, adj f199,f200
  f202: cylinder r=12.7mm len=25.4mm, axis (-1,0,0), area 131.7mm2, adj f200,f203
  f203: cone r=12.7mm half-angle=76deg, axis (1,0,0), area 188mm2, adj f202,f205
  f204: cone r=10.16mm half-angle=76deg, axis (-1,0,0), area 188mm2, adj f205,f207
  f205: cylinder r=10.16mm len=20.32mm, axis (1,0,0), area 81.1mm2, adj f203,f204
  f206: plane 25.4x25.4mm, normal (-1,0,0), area 506.7mm2, adj f207
  f207: cylinder r=12.7mm len=52.45mm, axis (-1,0,0), area 4185.4mm2, adj f204,f206
  f208: plane 6.88x5.08mm, normal (1,0,0), area 32.7mm2, adj f0,f4,f209,f210
  f209: plane 6.62x2.54mm, normal (0,-1,0), area 16.8mm2, adj f0,f3,f4,f208
  f210: plane 6.62x2.54mm, normal (0,1,0), area 16.8mm2, adj f0,f2,f4,f208
  f211: plane 6.88x5.08mm, normal (1,0,0), area 32.7mm2, adj f0,f4,f212,f213
  f212: plane 6.62x2.54mm, normal (0,0,1), area 16.8mm2, adj f0,f3,f4,f211
  f213: plane 6.62x2.54mm, normal (0,0,-1), area 16.8mm2, adj f0,f1,f4,f211
  f214: plane 6.88x5.08mm, normal (1,0,0), area 32.7mm2, adj f0,f4,f215,f216
  f215: plane 6.62x2.54mm, normal (0,1,0), area 16.8mm2, adj f0,f4,f5,f214
  f216: plane 6.62x2.54mm, normal (0,-1,0), area 16.8mm2, adj f0,f1,f4,f214
  f217: plane 6.62x2.54mm, normal (0,0,-1), area 16.8mm2, adj f0,f4,f5,f219
  f218: plane 6.62x2.54mm, normal (0,0,1), area 16.8mm2, adj f0,f2,f4,f219
  f219: plane 6.88x5.08mm, normal (1,0,0), area 32.7mm2, adj f0,f4,f217,f218
PART E: 11 faces, bbox 76.2x172.7x34.4 mm
  f0: sphere r=10.16mm, area 1231.8mm2, adj f1
  f1: cylinder r=4.45mm len=51.82mm, axis (0,1,0), area 1438.5mm2, adj f0,f4
  f2: sphere r=10.16mm, area 1231.8mm2, adj f3
  f3: cylinder r=4.45mm len=51.82mm, axis (0,1,0), area 1438.5mm2, adj f2,f4
  f4: cylinder r=15.88mm len=31.75mm, axis (-1,0,0), area 2534.7mm2, adj f1,f3,f9,f10
  f5: cylinder r=6.35mm len=44.45mm, axis (-1,0,0), area 1773.5mm2, adj f6,f8
  f6: plane 12.7x12.7mm, normal (-1,0,0), area 126.7mm2, adj f5
  f7: plane 26.67x26.67mm, normal (1,0,0), area 558.6mm2, adj f10
  f8: plane 26.67x26.67mm, normal (-1,0,0), area 432mm2, adj f5,f9
  f9: torus R=13.33mm, axis (1,0,0), area 374.8mm2, adj f4,f8
  f10: torus R=13.33mm, axis (1,0,0), area 374.8mm2, adj f4,f7
PLACE A at identity
PLACE B rot(axis=(0,0,1),90deg) t=(-254,-88.9,9.52)mm
PLACE C at identity fixed
PLACE D rot(axis=(1,0,0),180deg) t=(0,0,152.4)mm
PLACE E rot(axis=(1,0,0),180deg) t=(-21.59,0,152.4)mm
MATE fastened D.f4 <-> E.f5  axis (1,0,0) through (16.51,0,76.2)mm
MATE planar A.f0 <-> C.f2  axis (0,0,-1) through (-244.48,-38.1,38.1)mm
MATE pin_slot B.f1 <-> C.f41  axis (0,0,1) through (-254,-88.9,9.52)mm
MATE revolute D.f7 <-> A.f28  axis (-1,0,0) through (-260.35,0,76.2)mm
MATE cylindrical C.f12 <-> D.f7  axis (-1,0,0) through (-38.1,0,76.2)mm
